# Revit family: Slim Round 440 Suspended
name_source: partatom
category: Lighting Fixtures
revit_build: Autodesk Revit 2015 (Build: 20160512_1515(x64)
units: mm (PartAtom-declared; Revit-internal decimal feet)

## types (1)
- Slim Round 440 Suspended
    Body Finish = Louis Poulsen - ALU GREY - 351
    Color Filter = 16777215
    Default Elevation = 1000 mm  [stored 3.28084 ft]
    Description = x
    Dimming Lamp Color Temperature Shift = <None>
    Height = 0 mm  [stored 0 ft]
    Lamp = x
    Length = 0 mm  [stored 0 ft]
    Manufacturer = Louis Poulsen Lighting
    Number of Poles (US Only) = 0
    Photometric Web File = generic
    Power Factor (US Only) = 0
    Product Category = Pendant
    Product Code = x
    Reflector Finish = <By Category>
    Tilt Angle = -90.00°
    Voltage (US Only) = 0 V
    Weight (Kg) = 0
    Width = 0 mm  [stored 0 ft]

note: [stored X ft] marks values corroborated as IEEE doubles in the binary element streams (Revit-internal decimal feet)

## geometry (parser evidence)
native form markers: Sweep x3
no freeform markers — native parametric forms only
